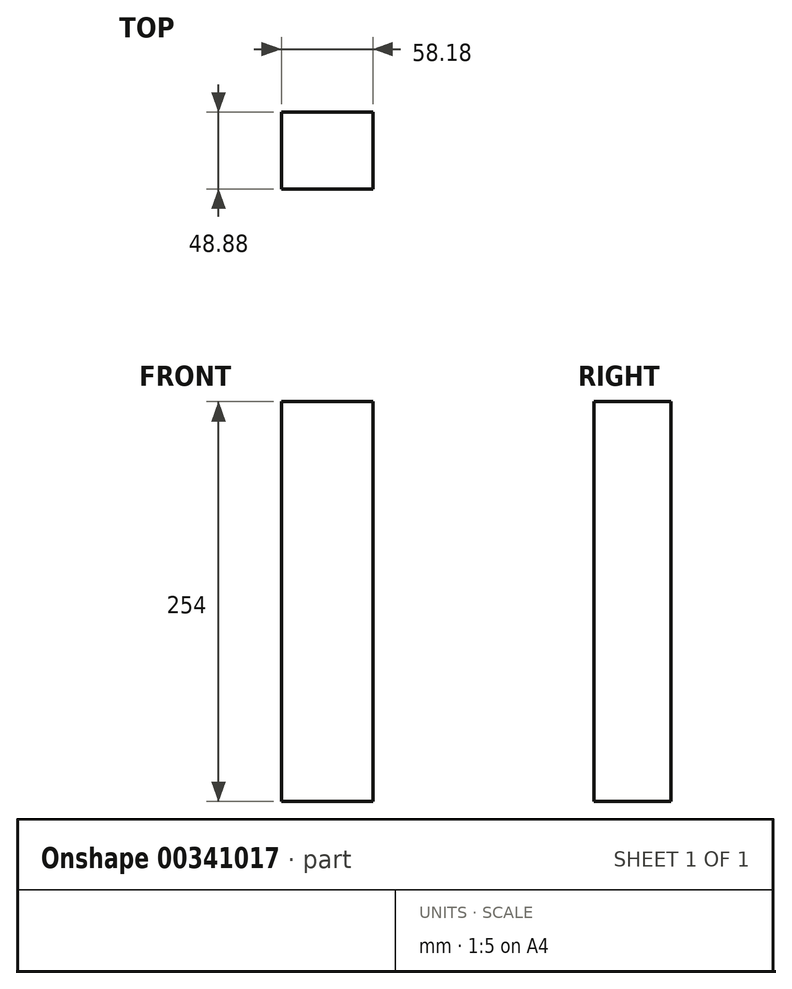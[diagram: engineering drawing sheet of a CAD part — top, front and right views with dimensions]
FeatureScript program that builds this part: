
annotation { "Feature Type Name" : "Feature", "Feature Type Description" : "" }
export const myFeature = defineFeature(function(context is Context, id is Id, definition is map)
    precondition{}
    {
        {
            var Q0;
            Q0=qCreatedBy(makeId("Top.planeOp"),FACE);
            var sketch = newSketch(context, id + "F0", { "sketchPlane" : qUnion([Q0])});
            skLineSegment(sketch, "E0", {"start": v(0, 0) * mm, "end": v(0, 48.88) * mm});
            skLineSegment(sketch, "E1", {"start": v(0, 48.88) * mm, "end": v(58.18, 48.88) * mm});
            skLineSegment(sketch, "E2", {"start": v(58.18, 48.88) * mm, "end": v(58.18, 0) * mm});
            skLineSegment(sketch, "E3", {"start": v(58.18, 0) * mm, "end": v(0, 0) * mm});
            skSolve(sketch);
        }
        {
            var Q0;
            Q0 = qSketchRegion(id + "F0", true);
            var Q1;
            Q1=makeQuery(id+"F0.imprint","IMPRINT",FACE,{"disambiguationData":[TD([[makeQuery(id+"F0.imprint","IMPRINT",EDGE,{"derivedFrom":sQuery(id+"F0.wireOp",EDGE,"E0")}),-1.0]])]});
            extrude(context, id + "F1", {"entities" : qUnion([Q0, Q1]), "depth" : 254 * mm});
        }
        {
            var Q0;
            Q0=makeQuery(id+"F1.opExtrude","CAP_FACE",FACE,{"disambiguationData":[OSD([sQuery(id+"F0.wireOp",EDGE,"E0"),sQuery(id+"F0.wireOp",EDGE,"E1"),sQuery(id+"F0.wireOp",EDGE,"E2"),sQuery(id+"F0.wireOp",EDGE,"E3")])],"isStart":false});
            extrude(context, id + "F2", {"entities" : qUnion([Q0]), "operationType" : NewBodyOperationType.ADD, "oppositeDirection" : true, "depth" : 127 * mm});
        }
    });
